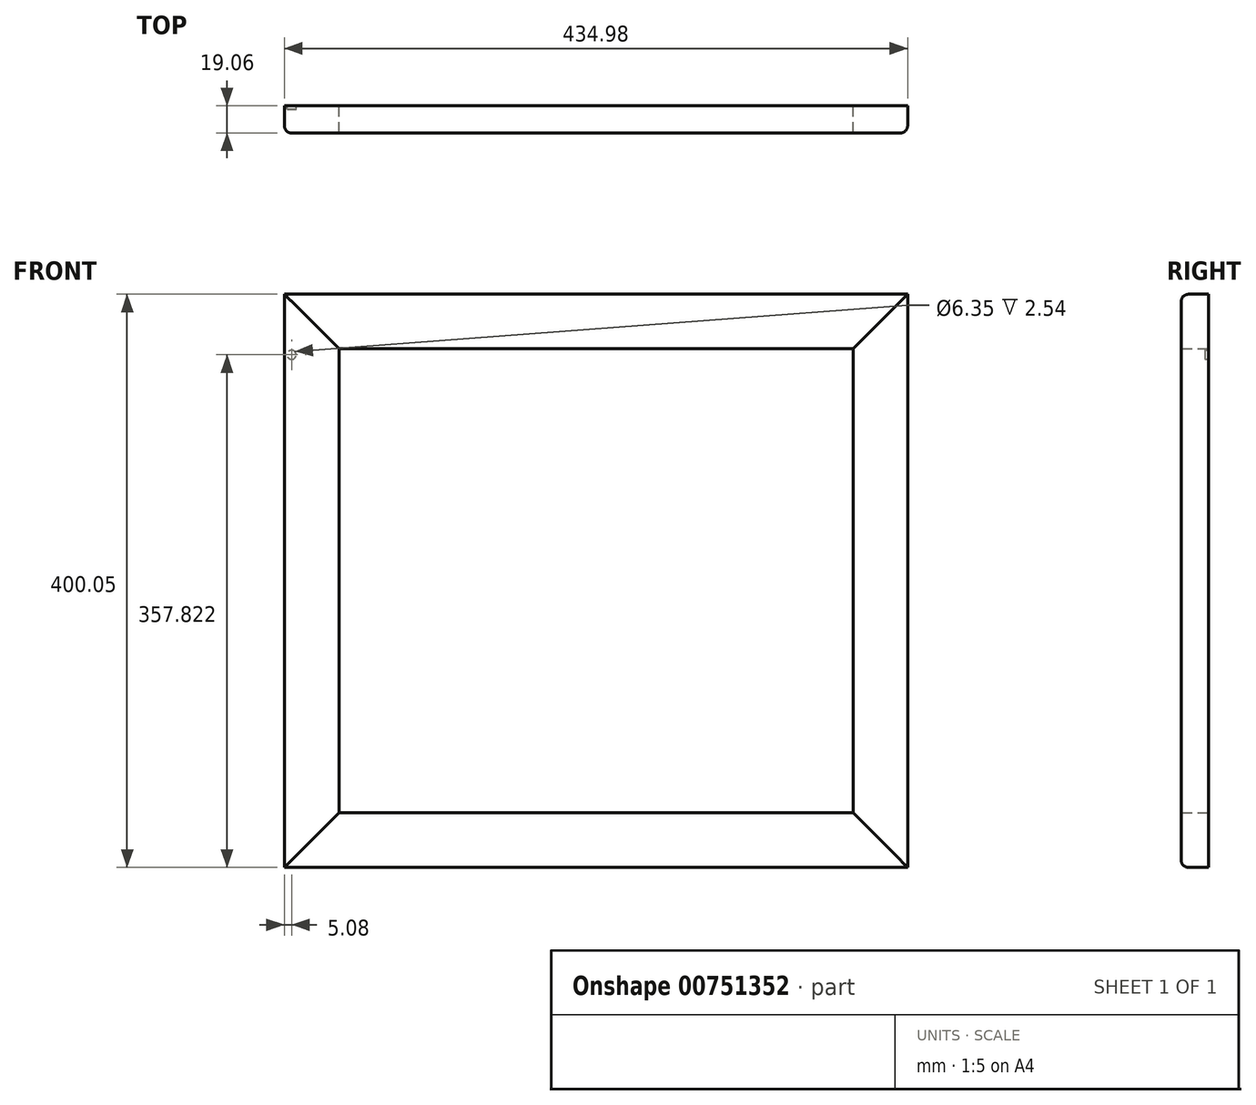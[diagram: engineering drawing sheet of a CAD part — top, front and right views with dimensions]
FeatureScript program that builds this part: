
annotation { "Feature Type Name" : "Feature", "Feature Type Description" : "" }
export const myFeature = defineFeature(function(context is Context, id is Id, definition is map)
    precondition{}
    {
        {
            assignVariable(context, id + "F0", {"name" : "thickness", "anyValue" : 19.05 * mm});
        }
        {
            var Q0;
            Q0=qCreatedBy(makeId("Front.planeOp"),FACE);
            var sketch = newSketch(context, id + "F1", { "sketchPlane" : qUnion([Q0])});
            skLineSegment(sketch, "E0.left", {"start": v(0, 0) * mm, "end": v(0, 400.05) * mm});
            skLineSegment(sketch, "E0.right", {"start": v(38.1, 38.1) * mm, "end": v(38.1, 361.95) * mm});
            skLineSegment(sketch, "E1", {"start": v(0, 400.05) * mm, "end": v(38.1, 361.95) * mm});
            skLineSegment(sketch, "E2", {"start": v(0, 0) * mm, "end": v(38.1, 38.1) * mm});
            skSolve(sketch);
        }
        {
            var Q0;
            Q0 = qSketchRegion(id + "F1", true);
            extrude(context, id + "F2", {"entities" : qUnion([Q0]), "endBound" : BoundingType.SYMMETRIC, "depth" : getVariable(context, 'thickness'), "offsetDistance" : 25.4 * mm});
        }
        {
            var Q0;
            Q0=qCreatedBy(makeId("Front.planeOp"),FACE);
            var sketch = newSketch(context, id + "F3", { "sketchPlane" : qUnion([Q0])});
            skLineSegment(sketch, "E3.bottom", {"start": v(0, 0) * mm, "end": v(434.98, 0) * mm});
            skLineSegment(sketch, "E3.top", {"start": v(38.1, 38.1) * mm, "end": v(396.88, 38.1) * mm});
            skLineSegment(sketch, "E4", {"start": v(0, 0) * mm, "end": v(38.1, 38.1) * mm});
            skLineSegment(sketch, "E5", {"start": v(434.98, 0) * mm, "end": v(396.88, 38.1) * mm});
            skSolve(sketch);
        }
        {
            var Q0;
            Q0 = qSketchRegion(id + "F3", true);
            extrude(context, id + "F4", {"entities" : qUnion([Q0]), "endBound" : BoundingType.SYMMETRIC, "depth" : 19.05 * mm, "offsetDistance" : 25.4 * mm});
        }
        {
            var Q0;
            Q0=makeQuery(id+"F4.opExtrude","CAP_EDGE",EDGE,{"disambiguationData":[OSD([sQuery(id+"F3.wireOp",EDGE,"E3.top")])],"isStart":false});
            cPoint(context, id + "F5", {"entities" : qUnion([Q0]), "parameter" : 0.5});
        }
        {
            var Q0;
            Q0=qCreatedBy(makeId("Right.planeOp"),FACE);
            var Q1;
            Q1 = qCreatedBy(id + "F5" ,VERTEX);
            cPlane(context, id + "F6", {"entities" : qUnion([Q0, Q1]), "cplaneType" : CPlaneType.PLANE_POINT, "offset" : 25.4 * mm, "width" : 152.4 * mm, "height" : 152.4 * mm});
        }
        {
            var Q0;
            Q0=makeQuery(id+"F2.opExtrude","SWEPT_BODY",BODY,{"disambiguationData":[OSD([sQuery(id+"F1.wireOp",EDGE,"E0.left"),sQuery(id+"F1.wireOp",EDGE,"E0.right"),sQuery(id+"F1.wireOp",EDGE,"E1"),sQuery(id+"F1.wireOp",EDGE,"E2")])]});
            var Q1;
            Q1=qCreatedBy(id+"F6.planeOp",FACE);
            mirror(context, id + "F7", {"entities" : qUnion([Q0]), "mirrorPlane" : qUnion([Q1])});
        }
        {
            var Q0;
            Q0=makeQuery(id+"F2.opExtrude","CAP_EDGE",EDGE,{"disambiguationData":[OSD([sQuery(id+"F1.wireOp",EDGE,"E0.left")])],"isStart":false});
            cPoint(context, id + "F8", {"entities" : qUnion([Q0]), "parameter" : 0.5});
        }
        {
            var Q0;
            Q0=qCreatedBy(makeId("Top.planeOp"),FACE);
            var Q1;
            Q1 = qCreatedBy(id + "F8" ,VERTEX);
            cPlane(context, id + "F9", {"entities" : qUnion([Q0, Q1]), "cplaneType" : CPlaneType.PLANE_POINT, "offset" : 25.4 * mm, "width" : 152.4 * mm, "height" : 152.4 * mm});
        }
        {
            var Q0;
            Q0=makeQuery(id+"F4.opExtrude","SWEPT_BODY",BODY,{"disambiguationData":[OSD([sQuery(id+"F3.wireOp",EDGE,"E3.bottom"),sQuery(id+"F3.wireOp",EDGE,"E3.top"),sQuery(id+"F3.wireOp",EDGE,"E4"),sQuery(id+"F3.wireOp",EDGE,"E5")])]});
            var Q1;
            Q1=qCreatedBy(id+"F9.planeOp",FACE);
            mirror(context, id + "F10", {"entities" : qUnion([Q0]), "mirrorPlane" : qUnion([Q1])});
        }
        {
            var Q0;
            Q0=makeQuery(id+"F2.opExtrude","CAP_FACE",FACE,{"disambiguationData":[OSD([sQuery(id+"F1.wireOp",EDGE,"E0.left"),sQuery(id+"F1.wireOp",EDGE,"E0.right"),sQuery(id+"F1.wireOp",EDGE,"E1"),sQuery(id+"F1.wireOp",EDGE,"E2")])],"isStart":true});
            var sketch = newSketch(context, id + "F11", { "sketchPlane" : qUnion([Q0])});
            skCircle(sketch, "E6", {"center": v(-5.08, 357.82) * mm, "radius": 3.18 * mm});
            skSolve(sketch);
        }
        {
            var Q0;
            Q0 = qSketchRegion(id + "F11", true);
            extrude(context, id + "F12", {"entities" : qUnion([Q0]), "operationType" : NewBodyOperationType.REMOVE, "oppositeDirection" : true, "depth" : 2.54 * mm, "offsetDistance" : 25.4 * mm});
        }
        {
            var Q0;
            Q0=makeQuery(id+"F2.opExtrude","CAP_EDGE",EDGE,{"disambiguationData":[OSD([sQuery(id+"F1.wireOp",EDGE,"E0.left")])],"isStart":false});
            var Q1;
            Q1=makeQuery(id+"F4.opExtrude","CAP_EDGE",EDGE,{"disambiguationData":[OSD([sQuery(id+"F3.wireOp",EDGE,"E3.bottom")])],"isStart":false});
            var Q2;
            Q2=makeQuery(id+"F7.opPattern","COPY",EDGE,{"derivedFrom":makeQuery(id+"F2.opExtrude","CAP_EDGE",EDGE,{"disambiguationData":[OSD([sQuery(id+"F1.wireOp",EDGE,"E0.left")])],"isStart":false}),"instanceName":"1"});
            var Q3;
            Q3=makeQuery(id+"F10.opPattern","COPY",EDGE,{"derivedFrom":makeQuery(id+"F4.opExtrude","CAP_EDGE",EDGE,{"disambiguationData":[OSD([sQuery(id+"F3.wireOp",EDGE,"E3.bottom")])],"isStart":false}),"instanceName":"1"});
            fillet(context, id + "F13", {"entities" : qUnion([Q0, Q1, Q2, Q3]), "radius" : 5.08 * mm, "tangentPropagation" : true, "allowEdgeOverflow" : false});
        }
    });
